# Revit family: 71_98_0131_NESTED
name_source: partatom
category: Communication Devices
revit_build: Autodesk Revit 2015 (Build: 20140606_1530(x64)
units: mm (PartAtom-declared; Revit-internal decimal feet)

## types (3) — shared parameters
Basisplaat = Basisplaat
Breedte = 160 mm  [stored 0.524934 ft]
Consumption = 5 W
Default Elevation = 1219 mm
Diepte = 70 mm  [stored 0.229659 ft]
Dynamic range = > 90 dB
Frequency response = 200-20,000 Hz
Jack = Jack
Kabel = Kabel
Knoppen = Basisplaat
Lengte = 220 mm  [stored 0.721785 ft]
Load impedance = 8 Ω
Manufacturer = Televic Conference
Maximum output power = > 1 W
Model = Confidea T-DIV
Onderplaat = Inox
Product ID = 71.98.0108
Scherm = Jack
Schroef = Basisplaat
Speaker = Jack
THD @ nominal level = < 0.1%
Type 71.98.0108 = Yes
Type Comments = Confidea Tabletop Delegate Interpretation & Voting Unit
URL = http://www.televic-conference.com
Voltage = 48 V
Weight = 480
lichten = Lichten

## per-type parameters (varying)
| type | Flexible microphone - 71.03.3540 | Microphone - 71.03.3140 |
| Type 71.98.0131 - no microphone | No | No |
| Type 71.98.0131 - microphone | No | Yes |
| Type 71.98.0131 - flexible microphone | Yes | No |

note: [stored X ft] marks values corroborated as IEEE doubles in the binary element streams (Revit-internal decimal feet)

## geometry (parser evidence)
native form markers: Sweep x17
no freeform markers — native parametric forms only
